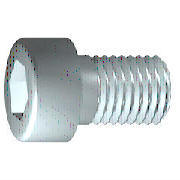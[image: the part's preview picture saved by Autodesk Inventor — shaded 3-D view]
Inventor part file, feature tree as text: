
AUTODESK INVENTOR PART (.ipt)
format: ipt  version: 2022 (Build 260153000, 153)  size: 196,608 bytes
history: native  units: mm (DEFAULTED — no unit token found)
features: sketch x2, other x1, extrude x1, plane x1, fillet x1
ambient origin geometry x7: Origin, YZ Plane, XY Plane, X Axis, Y Axis, Z Axis, Center Point
bodies: Solid1 (feature_tree)
feature tree (6):
  other  "Cuerpo"
  extrude  "Ranura"  Depth=3.0mm
  plane  "Work Plane1"
  fillet  "Fillet2"  Radius=3.0mm
  sketch  "Boceto1"  dims[d1=6.75mm d2=0.306825mm d3=3.0mm]
  sketch  "Boceto2"  dims[d4=1.3mm d5=60.0deg d6=3.0mm d7=3.0mm d8=2.886751mm d9=5.5mm d10=90.0deg d11=10.0mm d12=0.0mm d13=6.75mm d14=0.0mm d15=0.306725mm d16=0.306725mm d17=0.3mm d19=0.0mm d26=8.0mm d27=45.0deg d28=0.0mm d29=0.0mm d30=0.1mm]
